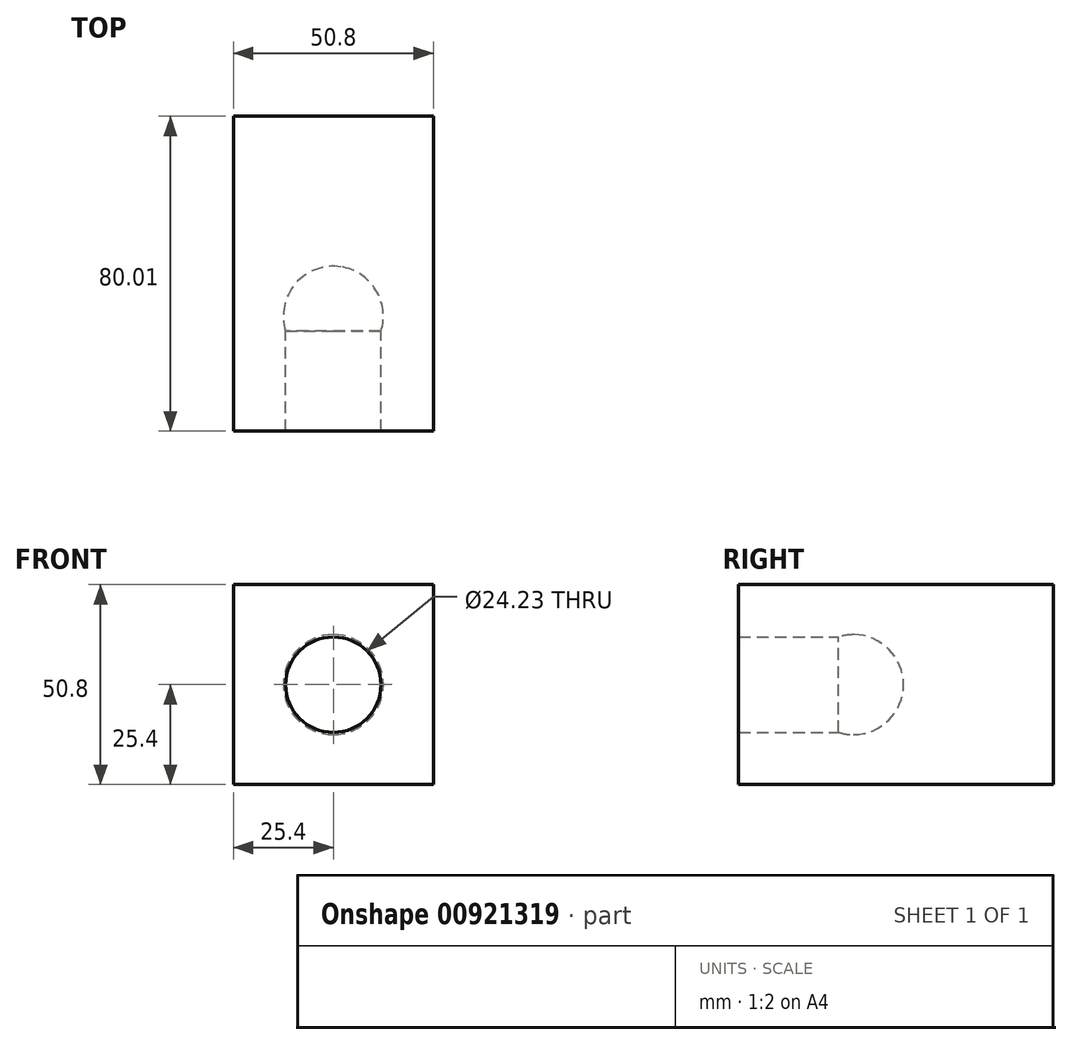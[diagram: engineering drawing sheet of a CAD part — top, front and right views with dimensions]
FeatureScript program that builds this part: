
annotation { "Feature Type Name" : "Feature", "Feature Type Description" : "" }
export const myFeature = defineFeature(function(context is Context, id is Id, definition is map)
    precondition{}
    {
        {
            var Q0;
            Q0=qCreatedBy(makeId("Front.planeOp"),FACE);
            var sketch = newSketch(context, id + "F0", { "sketchPlane" : qUnion([Q0])});
            skLineSegment(sketch, "E0", {"start": v(0, 80.03) * mm, "end": v(0, -94.1) * mm});
            skLineSegment(sketch, "E1.bottom", {"start": v(-25.4, 25.4) * mm, "end": v(25.4, 25.4) * mm});
            skLineSegment(sketch, "E1.top", {"start": v(-25.4, -25.4) * mm, "end": v(25.4, -25.4) * mm});
            skLineSegment(sketch, "E1.left", {"start": v(-25.4, 25.4) * mm, "end": v(-25.4, -25.4) * mm});
            skLineSegment(sketch, "E1.right", {"start": v(25.4, 25.4) * mm, "end": v(25.4, -25.4) * mm});
            skPoint(sketch, "E1.middle", {"position": v(0, 0) * mm});
            skSolve(sketch);
        }
        {
            var Q0;
            {var subQ5=sQuery(id+"F0.wireOp",EDGE,"E1.left");Q0=makeQuery(id+"F0.imprint","IMPRINT",FACE,{"disambiguationData":[TD([[makeQuery(id+"F0.imprint","IMPRINT",EDGE,{"derivedFrom":subQ5}),1.0]])]});}
            var Q1;
            {var subQ5=sQuery(id+"F0.wireOp",EDGE,"E1.right");Q1=makeQuery(id+"F0.imprint","IMPRINT",FACE,{"disambiguationData":[TD([[makeQuery(id+"F0.imprint","IMPRINT",EDGE,{"derivedFrom":subQ5}),-1.0]])]});}
            extrude(context, id + "F1", {"entities" : qUnion([Q0, Q1]), "endBound" : BoundingType.SYMMETRIC, "depth" : 50.8 * mm, "offsetDistance" : 25.4 * mm});
        }
        {
            var Q0;
            Q0=makeQuery(id+"F1.opExtrude","CAP_FACE",FACE,{"disambiguationData":[OSD([sQuery(id+"F0.wireOp",EDGE,"E1.bottom"),sQuery(id+"F0.wireOp",EDGE,"E1.top"),sQuery(id+"F0.wireOp",EDGE,"E1.left"),sQuery(id+"F0.wireOp",EDGE,"E1.right")])],"isStart":false});
            var sketch = newSketch(context, id + "F2", { "sketchPlane" : qUnion([Q0])});
            skCircle(sketch, "E2", {"center": v(0, 0) * mm, "radius": 12.7 * mm});
            skLineSegment(sketch, "E3", {"start": v(0, 43.8) * mm, "end": v(0, -58.6) * mm});
            skSolve(sketch);
        }
        {
            var Q0;
            {var subQ8=makeQuery(id+"F1.opExtrude","CAP_EDGE",EDGE,{"disambiguationData":[OSD([sQuery(id+"F0.wireOp",EDGE,"E1.left")])],"isStart":false});Q0=makeQuery(id+"F2.imprint","IMPRINT",FACE,{"disambiguationData":[TD([[makeQuery(id+"F2.imprint","IMPRINT",EDGE,{"derivedFrom":subQ8}),1.0]])]});}
            var Q1;
            {var subQ8=makeQuery(id+"F1.opExtrude","CAP_EDGE",EDGE,{"disambiguationData":[OSD([sQuery(id+"F0.wireOp",EDGE,"E1.right")])],"isStart":false});Q1=makeQuery(id+"F2.imprint","IMPRINT",FACE,{"disambiguationData":[TD([[makeQuery(id+"F2.imprint","IMPRINT",EDGE,{"derivedFrom":subQ8}),-1.0]])]});}
            var Q2;
            {var subQ0=sQuery(id+"F2.wireOp",EDGE,"E3");var subQ1=sQuery(id+"F2.wireOp",EDGE,"E2");var subQ2=makeQuery(id+"F2.imprint","INTERSECT",VERTEX,{"disambiguationData":[OD(0.0)],"derivedFrom":[subQ1,subQ0]});Q2=makeQuery(id+"F2.imprint","IMPRINT",FACE,{"disambiguationData":[TD([[makeQuery(id+"F2.imprint","IMPRINT",EDGE,{"disambiguationData":[TD([[subQ2,-1.0]])],"derivedFrom":subQ1}),1.0]])]});}
            var Q3;
            {var subQ0=sQuery(id+"F2.wireOp",EDGE,"E3");var subQ1=sQuery(id+"F2.wireOp",EDGE,"E2");var subQ2=makeQuery(id+"F2.imprint","INTERSECT",VERTEX,{"disambiguationData":[OD(0.0)],"derivedFrom":[subQ1,subQ0]});Q3=makeQuery(id+"F2.imprint","IMPRINT",FACE,{"disambiguationData":[TD([[makeQuery(id+"F2.imprint","IMPRINT",EDGE,{"disambiguationData":[TD([[subQ2,1.0]])],"derivedFrom":subQ1}),1.0]])]});}
            extrude(context, id + "F3", {"entities" : qUnion([Q0, Q1, Q2, Q3]), "operationType" : NewBodyOperationType.ADD, "depth" : 25.4 * mm, "offsetDistance" : 25.4 * mm});
        }
        {
            var Q0;
            {var subQ0=sQuery(id+"F2.wireOp",EDGE,"E3");var subQ1=sQuery(id+"F2.wireOp",EDGE,"E2");var subQ2=makeQuery(id+"F2.imprint","INTERSECT",VERTEX,{"disambiguationData":[OD(0.0)],"derivedFrom":[subQ1,subQ0]});Q0=makeQuery(id+"F2.imprint","IMPRINT",FACE,{"disambiguationData":[TD([[makeQuery(id+"F2.imprint","IMPRINT",EDGE,{"disambiguationData":[TD([[subQ2,-1.0]])],"derivedFrom":subQ1}),1.0]])]});}
            var Q1;
            Q1=sQuery(id+"F2.wireOp",EDGE,"E3");
            revolve(context, id + "F4", {"operationType" : NewBodyOperationType.REMOVE, "surfaceOperationType" : NewSurfaceOperationType.NEW, "entities" : qUnion([Q0]), "axis" : qUnion([Q1]), "revolveType" : RevolveType.FULL});
        }
        {
            var Q0;
            Q0=makeQuery(id+"F3.opExtrude","CAP_FACE",FACE,{"disambiguationData":[OSD([sQuery(id+"F0.wireOp",EDGE,"E1.bottom"),sQuery(id+"F0.wireOp",EDGE,"E1.top"),sQuery(id+"F0.wireOp",EDGE,"E1.left"),sQuery(id+"F0.wireOp",EDGE,"E1.right")])],"isStart":false});
            extrude(context, id + "F5", {"entities" : qUnion([Q0]), "operationType" : NewBodyOperationType.REMOVE, "oppositeDirection" : true, "depth" : 21.59 * mm, "offsetDistance" : 25.4 * mm});
        }
        {
            var Q0;
            Q0=makeQuery(id+"F5.boolean.opBoolean","COPY",FACE,{"derivedFrom":makeQuery(id+"F5.opExtrude","CAP_FACE",FACE,{"disambiguationData":[OSD([sQuery(id+"F0.wireOp",EDGE,"E1.bottom"),sQuery(id+"F0.wireOp",EDGE,"E1.top"),sQuery(id+"F0.wireOp",EDGE,"E1.left"),sQuery(id+"F0.wireOp",EDGE,"E1.right")])],"isStart":false})});
            extrude(context, id + "F6", {"entities" : qUnion([Q0]), "operationType" : NewBodyOperationType.ADD, "depth" : 25.4 * mm, "offsetDistance" : 25.4 * mm});
        }
    });
